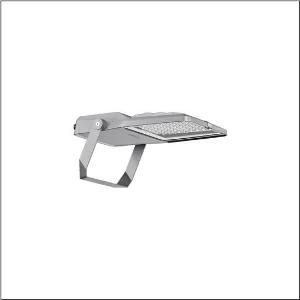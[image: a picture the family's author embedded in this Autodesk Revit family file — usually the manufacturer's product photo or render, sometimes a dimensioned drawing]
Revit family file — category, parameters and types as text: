
# Revit family: floodlight_fl_21_iq_mini___rs12_5xa7772c3b1a_483e
name_source: partatom
category: Lighting Fixtures
units: mm (PartAtom-declared; Revit-internal decimal feet)

## family parameters
Cut with Voids When Loaded = No
Host = Face
Light Source = No
Part Type = Normal
Room Calculation Point = No
Round Connector Dimension = Use Diameter
Shared = No

## types (1)
- --- (1 x LED, 10620 lm, 87.2 W, 3000K)
    Apparent Load = 87 VA
    CIE Flux Codes = 79 92 99 100 100
    Color Rendering = 80
    Color Temperature = 3000K
    Default Elevation = 1800 mm
    Description = Floodlight FL 21 iQ mini, floodlight, primary light control with lens, of PMMA, primary optical cover: protective disc, of toughened safety glass, transparent, light distribution: RS12, light emission: direct distribution, installation type: surface-mounted, LED, High Power LED, rated luminous flux: 10.620lm, luminous efficacy: 122lm/W, light colour: 830, colour temperature: 3000K, control: Street-Remote, Auto-Match, Temp-Guard, Night-Set, Smart-Wire, Desk-Remote (wireless, voltage-free reading and setting of iQ features in the workshop via application-optimized NFC function/RFID function), optimised constant luminous flux control (CLO 2.0), with terminal, 6-pole, mains connection: 220..240V, AC, 50/60Hz, start of lifetime: 87W, end of service life: 92W, reduction: 40W, luminaire housing, of diecast aluminium, powder-coated, Siteco® metallic grey (DB 702S), corrosivity category C5 mid according to DIN EN ISO 12944, sealing non-destructively replaceable, mounting bracket, of steel, galvanised, powder-coated, Siteco® metallic grey (DB 702S), protection rating (complete): IP66, insulation class (complete): insulation class II (safety insulation), certification: CE, ENEC, VDE, protection symbol: D, impact resistance: IK08, permissible operating ambient temperature: -40..+40°C, permissible operating ambient temperature for outdoor applications: -40..+50°C, standard: DIN EN 12944, LABS conformity tested according to VDMA 24364:2018-05, packaging unit: 1 piece

Light Distribution: RS12
    Height = 70 mm
    Lamp = 1 x LED
    Lamp Light Flux = 10620 lm
    Lamp Power = 87.2 W
    Lamp count = 1
    Length = 485 mm
    Luminous efficacy = 122 lm/W
    Manufacturer = Siteco
    ModVariant = No
    Model = 5XA7772C3B1A
    Number of Poles = 1
    OnlyDefault = Yes
    Power Factor = 1
    Product Name = Floodlight FL 21 iQ mini | RS12
    Product group = floodlight | pylon annexe
    ProductGroupID = 6200
    Protection Class = Protection class II
    Protection Degree = IP 66
    RLX_Detail_Level = 1
    RLX_Emergency_Light_Flux = 0 lm
    RLX_Emergency_Type = 0
    RLX_Emergency_Type_DB = No
    RlxData = <blob elided: 90877 chars, md5=81c02d76>
    Socket = socket
    Standby Power = 0 W
    System Light Flux = 10620 lm
    System Power = 87 W
    Type Comments = factory setting: luminous flux: 100 % | dim-lin: 254 | 456 mA
    Type Image = l_1006845.jpg
    URL = http://relux.com
    VarID = @adj_099915
    Voltage = 0 V
    Weight = 0.00 kg
    Width = 337 mm

## geometry (parser evidence)
native form markers: Blend x4, Sweep x16
no freeform markers — native parametric forms only
